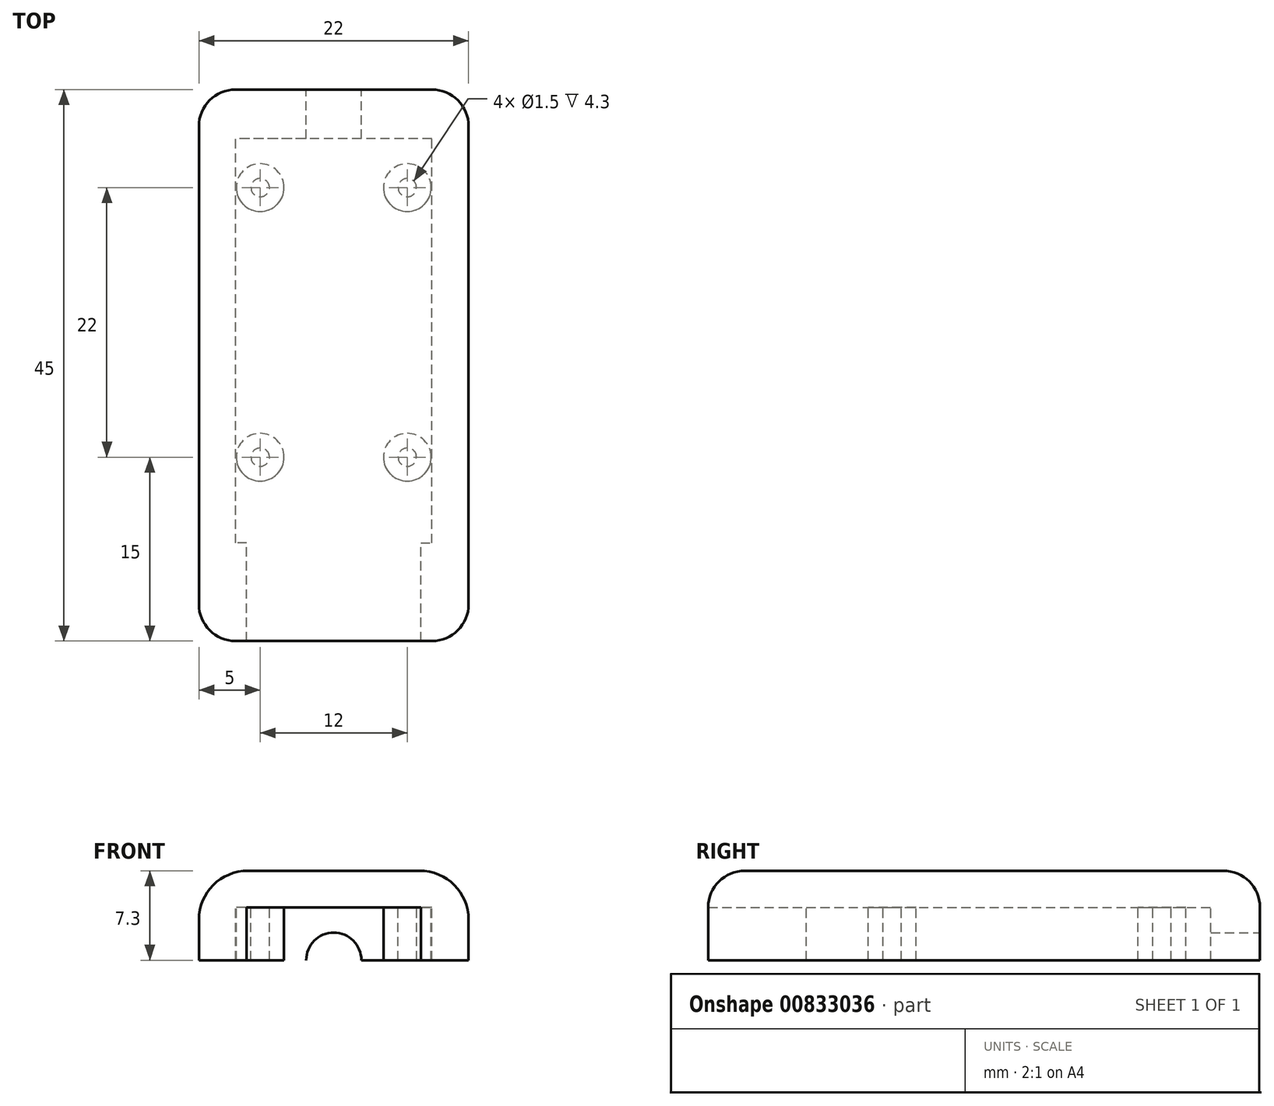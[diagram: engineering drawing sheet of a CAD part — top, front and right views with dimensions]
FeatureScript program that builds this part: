
annotation { "Feature Type Name" : "Feature", "Feature Type Description" : "" }
export const myFeature = defineFeature(function(context is Context, id is Id, definition is map)
    precondition{}
    {
        {
            var Q0;
            Q0=qCreatedBy(makeId("Front.planeOp"),FACE);
            var sketch = newSketch(context, id + "F0", { "sketchPlane" : qUnion([Q0])});
            skLineSegment(sketch, "E0.top", {"start": v(0, 4.3) * mm, "end": v(16, 4.3) * mm});
            skLineSegment(sketch, "E0.left", {"start": v(0, 0) * mm, "end": v(0, 4.3) * mm});
            skLineSegment(sketch, "E0.right", {"start": v(16, 0) * mm, "end": v(16, 4.3) * mm});
            skLineSegment(sketch, "E1.0", {"start": v(-3, 0) * mm, "end": v(-3, 7.3) * mm});
            skLineSegment(sketch, "E2.0", {"start": v(19, 0) * mm, "end": v(19, 7.3) * mm});
            skLineSegment(sketch, "E3.0", {"start": v(-3, 7.3) * mm, "end": v(19, 7.3) * mm});
            skLineSegment(sketch, "E4", {"start": v(-3, 0) * mm, "end": v(0, 0) * mm});
            skLineSegment(sketch, "E5", {"start": v(16, 0) * mm, "end": v(19, 0) * mm});
            skSolve(sketch);
        }
        {
            var Q0;
            Q0=makeQuery(id+"F0.imprint","IMPRINT",FACE,{"disambiguationData":[TD([[makeQuery(id+"F0.imprint","IMPRINT",EDGE,{"derivedFrom":sQuery(id+"F0.wireOp",EDGE,"E0.top")}),1.0]])]});
            extrude(context, id + "F1", {"entities" : qUnion([Q0]), "depth" : 45 * mm, "offsetDistance" : 25 * mm});
        }
        {
            var Q0;
            Q0=makeQuery(id+"F1.opExtrude","SWEPT_FACE",FACE,{"disambiguationData":[OSD([sQuery(id+"F0.wireOp",EDGE,"E0.top")])]});
            var sketch = newSketch(context, id + "F2", { "sketchPlane" : qUnion([Q0])});
            skLineSegment(sketch, "E6.0", {"start": v(2, 30) * mm, "end": v(2, 0) * mm, "construction": true});
            skLineSegment(sketch, "E7.0", {"start": v(14, 30) * mm, "end": v(14, 0) * mm, "construction": true});
            skLineSegment(sketch, "E8.0", {"start": v(0, 30) * mm, "end": v(14, 30) * mm, "construction": true});
            skLineSegment(sketch, "E9.0", {"start": v(0, 8) * mm, "end": v(14.2, 8) * mm, "construction": true});
            skCircle(sketch, "E10", {"center": v(2, 30) * mm, "radius": 0.75 * mm});
            skCircle(sketch, "E11", {"center": v(14, 30) * mm, "radius": 0.75 * mm});
            skCircle(sketch, "E12", {"center": v(14, 8) * mm, "radius": 0.75 * mm});
            skCircle(sketch, "E13", {"center": v(2, 8) * mm, "radius": 0.75 * mm});
            skCircle(sketch, "E14", {"center": v(2, 30) * mm, "radius": 1.95 * mm});
            skCircle(sketch, "E15", {"center": v(14, 30) * mm, "radius": 1.95 * mm});
            skCircle(sketch, "E16", {"center": v(2, 8) * mm, "radius": 1.95 * mm});
            skCircle(sketch, "E17", {"center": v(14, 8) * mm, "radius": 1.95 * mm});
            skSolve(sketch);
        }
        {
            var Q0;
            Q0=makeQuery(id+"F1.opExtrude","SWEPT_FACE",FACE,{"disambiguationData":[OSD([sQuery(id+"F0.wireOp",EDGE,"E0.left")])]});
            var sketch = newSketch(context, id + "F3", { "sketchPlane" : qUnion([Q0])});
            skLineSegment(sketch, "E18.0", {"start": v(-4, 0) * mm, "end": v(-4, 4.3) * mm});
            skSolve(sketch);
        }
        {
            var Q0;
            {var subQ0=sQuery(id+"F3.wireOp",EDGE,"E18.0");Q0=makeQuery(id+"F3.imprint","IMPRINT",FACE,{"disambiguationData":[TD([[makeQuery(id+"F3.imprint","IMPRINT",EDGE,{"derivedFrom":subQ0}),-1.0]])]});}
            extrude(context, id + "F4", {"entities" : qUnion([Q0]), "operationType" : NewBodyOperationType.ADD, "depth" : 16 * mm, "offsetDistance" : 25 * mm});
        }
        {
            var Q0;
            {var subQ0=sQuery(id+"F0.wireOp",EDGE,"E0.left");Q0=makeQuery(id+"F4.boolean.opBoolean","MERGE",FACE,{"derivedFrom":[makeQuery(id+"F1.opExtrude","CAP_FACE",FACE,{"disambiguationData":[OSD([sQuery(id+"F0.wireOp",EDGE,"E0.top"),subQ0,sQuery(id+"F0.wireOp",EDGE,"E0.right"),sQuery(id+"F0.wireOp",EDGE,"E1.0"),sQuery(id+"F0.wireOp",EDGE,"E2.0"),sQuery(id+"F0.wireOp",EDGE,"E3.0"),sQuery(id+"F0.wireOp",EDGE,"E4"),sQuery(id+"F0.wireOp",EDGE,"E5")])],"isStart":true}),makeQuery(id+"F4.opExtrude","SWEPT_FACE",FACE,{"disambiguationData":[OSD([subQ0])]})]});}
            var sketch = newSketch(context, id + "F5", { "sketchPlane" : qUnion([Q0])});
            skLineSegment(sketch, "E19.0", {"start": v(-8, 0) * mm, "end": v(-8, 7.3) * mm});
            skCircle(sketch, "E20", {"center": v(-8, 0) * mm, "radius": 2.25 * mm});
            skSolve(sketch);
        }
        {
            var Q0;
            Q0=sQuery(id+"F5.wireOp",VERTEX,"E19.0.start");
            var Q1;
            Q1=makeQuery(id+"F1.opExtrude","SWEPT_BODY",BODY,{"disambiguationData":[OSD([sQuery(id+"F0.wireOp",EDGE,"E0.top"),sQuery(id+"F0.wireOp",EDGE,"E0.left"),sQuery(id+"F0.wireOp",EDGE,"E0.right"),sQuery(id+"F0.wireOp",EDGE,"E1.0"),sQuery(id+"F0.wireOp",EDGE,"E2.0"),sQuery(id+"F0.wireOp",EDGE,"E3.0"),sQuery(id+"F0.wireOp",EDGE,"E4"),sQuery(id+"F0.wireOp",EDGE,"E5")])]});
            hole(context, id + "F6", {"style" : HoleStyle.SIMPLE, "endStyle" : HoleEndStyle.BLIND, "holeDiameter" : 4.5 * mm, "majorDiameter" : 5 * mm, "holeDepth" : 30 * mm, "isTappedThrough" : true, "tappedDepth" : 12 * mm, "tapClearance" : 3, "locations" : qUnion([Q0]), "scope" : qUnion([Q1])});
        }
        {
            var Q0;
            Q0=makeQuery(id+"F1.opExtrude","SWEPT_BODY",BODY,{"disambiguationData":[OSD([sQuery(id+"F0.wireOp",EDGE,"E0.top"),sQuery(id+"F0.wireOp",EDGE,"E0.left"),sQuery(id+"F0.wireOp",EDGE,"E0.right"),sQuery(id+"F0.wireOp",EDGE,"E1.0"),sQuery(id+"F0.wireOp",EDGE,"E2.0"),sQuery(id+"F0.wireOp",EDGE,"E3.0"),sQuery(id+"F0.wireOp",EDGE,"E4"),sQuery(id+"F0.wireOp",EDGE,"E5")])]});
            transform(context, id + "F7", {"entities" : qUnion([Q0]), "transformType" : TransformType.TRANSLATION_3D, "dx" : 31.9 * mm, "dy" : 0.1 * mm, "dz" : 0 * mm, "makeCopy" : true});
        }
        {
            var Q0;
            Q0=makeQuery(id+"F1.opExtrude","SWEPT_EDGE",EDGE,{"disambiguationData":[OSD([sQuery(id+"F0.wireOp",EDGE,"E1.0"),sQuery(id+"F0.wireOp",EDGE,"E3.0")])]});
            var Q1;
            Q1=makeQuery(id+"F1.opExtrude","SWEPT_EDGE",EDGE,{"disambiguationData":[OSD([sQuery(id+"F0.wireOp",EDGE,"E2.0"),sQuery(id+"F0.wireOp",EDGE,"E3.0")])]});
            fillet(context, id + "F8", {"entities" : qUnion([Q0, Q1]), "radius" : 4 * mm, "tangentPropagation" : true, "allowEdgeOverflow" : false});
        }
        {
            var Q0;
            Q0=makeQuery(id+"F7.opPattern","COPY",BODY,{"derivedFrom":makeQuery(id+"F1.opExtrude","SWEPT_BODY",BODY,{"disambiguationData":[OSD([sQuery(id+"F0.wireOp",EDGE,"E0.top"),sQuery(id+"F0.wireOp",EDGE,"E0.left"),sQuery(id+"F0.wireOp",EDGE,"E0.right"),sQuery(id+"F0.wireOp",EDGE,"E1.0"),sQuery(id+"F0.wireOp",EDGE,"E2.0"),sQuery(id+"F0.wireOp",EDGE,"E3.0"),sQuery(id+"F0.wireOp",EDGE,"E4"),sQuery(id+"F0.wireOp",EDGE,"E5")])]}),"instanceName":"1"});
            deleteBodies(context, id + "F9", {"entities" : qUnion([Q0])});
        }
        {
            var Q0;
            Q0=makeQuery(id+"F1.opExtrude","SWEPT_BODY",BODY,{"disambiguationData":[OSD([sQuery(id+"F0.wireOp",EDGE,"E0.top"),sQuery(id+"F0.wireOp",EDGE,"E0.left"),sQuery(id+"F0.wireOp",EDGE,"E0.right"),sQuery(id+"F0.wireOp",EDGE,"E1.0"),sQuery(id+"F0.wireOp",EDGE,"E2.0"),sQuery(id+"F0.wireOp",EDGE,"E3.0"),sQuery(id+"F0.wireOp",EDGE,"E4"),sQuery(id+"F0.wireOp",EDGE,"E5")])]});
            transform(context, id + "F10", {"entities" : qUnion([Q0]), "transformType" : TransformType.TRANSLATION_3D, "dx" : 35.6 * mm, "dy" : 1.7 * mm, "dz" : 0 * mm, "makeCopy" : true});
        }
        {
            var Q0;
            Q0=makeQuery(id+"F1.opExtrude","SWEPT_FACE",FACE,{"disambiguationData":[OSD([sQuery(id+"F0.wireOp",EDGE,"E0.left")])]});
            var sketch = newSketch(context, id + "F11", { "sketchPlane" : qUnion([Q0])});
            skLineSegment(sketch, "E21.0", {"start": v(-37, 0) * mm, "end": v(-37, 4.3) * mm});
            skSolve(sketch);
        }
        {
            var Q0;
            Q0 = qSketchRegion(id + "F11", true);
            var Q1;
            {var subQ0=sQuery(id+"F11.wireOp",EDGE,"E21.0");Q1=makeQuery(id+"F11.imprint","IMPRINT",FACE,{"disambiguationData":[TD([[makeQuery(id+"F11.imprint","IMPRINT",EDGE,{"derivedFrom":subQ0}),1.0]])]});}
            extrude(context, id + "F12", {"entities" : qUnion([Q0, Q1]), "operationType" : NewBodyOperationType.ADD, "depth" : 0.9 * mm, "offsetDistance" : 25 * mm});
        }
        {
            var Q0;
            Q0=makeQuery(id+"F1.opExtrude","SWEPT_FACE",FACE,{"disambiguationData":[OSD([sQuery(id+"F0.wireOp",EDGE,"E0.right")])]});
            var sketch = newSketch(context, id + "F13", { "sketchPlane" : qUnion([Q0])});
            skLineSegment(sketch, "E22.0", {"start": v(37, 0) * mm, "end": v(37, 4.3) * mm});
            skSolve(sketch);
        }
        {
            var Q0;
            Q0 = qSketchRegion(id + "F13", true);
            var Q1;
            {var subQ0=sQuery(id+"F13.wireOp",EDGE,"E22.0");Q1=makeQuery(id+"F13.imprint","IMPRINT",FACE,{"disambiguationData":[TD([[makeQuery(id+"F13.imprint","IMPRINT",EDGE,{"derivedFrom":subQ0}),-1.0]])]});}
            extrude(context, id + "F14", {"entities" : qUnion([Q0, Q1]), "operationType" : NewBodyOperationType.ADD, "depth" : 0.9 * mm, "offsetDistance" : 25 * mm});
        }
        {
            var Q0;
            Q0=makeQuery(id+"F1.opExtrude","CAP_EDGE",EDGE,{"disambiguationData":[OSD([sQuery(id+"F0.wireOp",EDGE,"E3.0")])],"isStart":false});
            var Q1;
            Q1=makeQuery(id+"F1.opExtrude","CAP_EDGE",EDGE,{"disambiguationData":[OSD([sQuery(id+"F0.wireOp",EDGE,"E3.0")])],"isStart":true});
            fillet(context, id + "F15", {"entities" : qUnion([Q0, Q1]), "radius" : 3 * mm, "tangentPropagation" : true, "allowEdgeOverflow" : false});
        }
        {
            var Q0;
            Q0=makeQuery(id+"F2.imprint","IMPRINT",FACE,{"disambiguationData":[TD([[makeQuery(id+"F2.imprint","IMPRINT",EDGE,{"derivedFrom":sQuery(id+"F2.wireOp",EDGE,"E10")}),-1.0]])]});
            var Q1;
            Q1=makeQuery(id+"F2.imprint","IMPRINT",FACE,{"disambiguationData":[TD([[makeQuery(id+"F2.imprint","IMPRINT",EDGE,{"derivedFrom":sQuery(id+"F2.wireOp",EDGE,"E11")}),-1.0]])]});
            var Q2;
            Q2=makeQuery(id+"F2.imprint","IMPRINT",FACE,{"disambiguationData":[TD([[makeQuery(id+"F2.imprint","IMPRINT",EDGE,{"derivedFrom":sQuery(id+"F2.wireOp",EDGE,"E13")}),-1.0]])]});
            var Q3;
            Q3=makeQuery(id+"F2.imprint","IMPRINT",FACE,{"disambiguationData":[TD([[makeQuery(id+"F2.imprint","IMPRINT",EDGE,{"derivedFrom":sQuery(id+"F2.wireOp",EDGE,"E12")}),-1.0]])]});
            extrude(context, id + "F16", {"entities" : qUnion([Q0, Q1, Q2, Q3]), "operationType" : NewBodyOperationType.ADD, "depth" : 4.3 * mm, "offsetDistance" : 25 * mm});
        }
        {
            var Q0;
            Q0=makeQuery(id+"F10.opPattern","COPY",BODY,{"derivedFrom":makeQuery(id+"F1.opExtrude","SWEPT_BODY",BODY,{"disambiguationData":[OSD([sQuery(id+"F0.wireOp",EDGE,"E0.top"),sQuery(id+"F0.wireOp",EDGE,"E0.left"),sQuery(id+"F0.wireOp",EDGE,"E0.right"),sQuery(id+"F0.wireOp",EDGE,"E1.0"),sQuery(id+"F0.wireOp",EDGE,"E2.0"),sQuery(id+"F0.wireOp",EDGE,"E3.0"),sQuery(id+"F0.wireOp",EDGE,"E4"),sQuery(id+"F0.wireOp",EDGE,"E5")])]}),"instanceName":"1"});
            deleteBodies(context, id + "F17", {"entities" : qUnion([Q0])});
        }
    });
